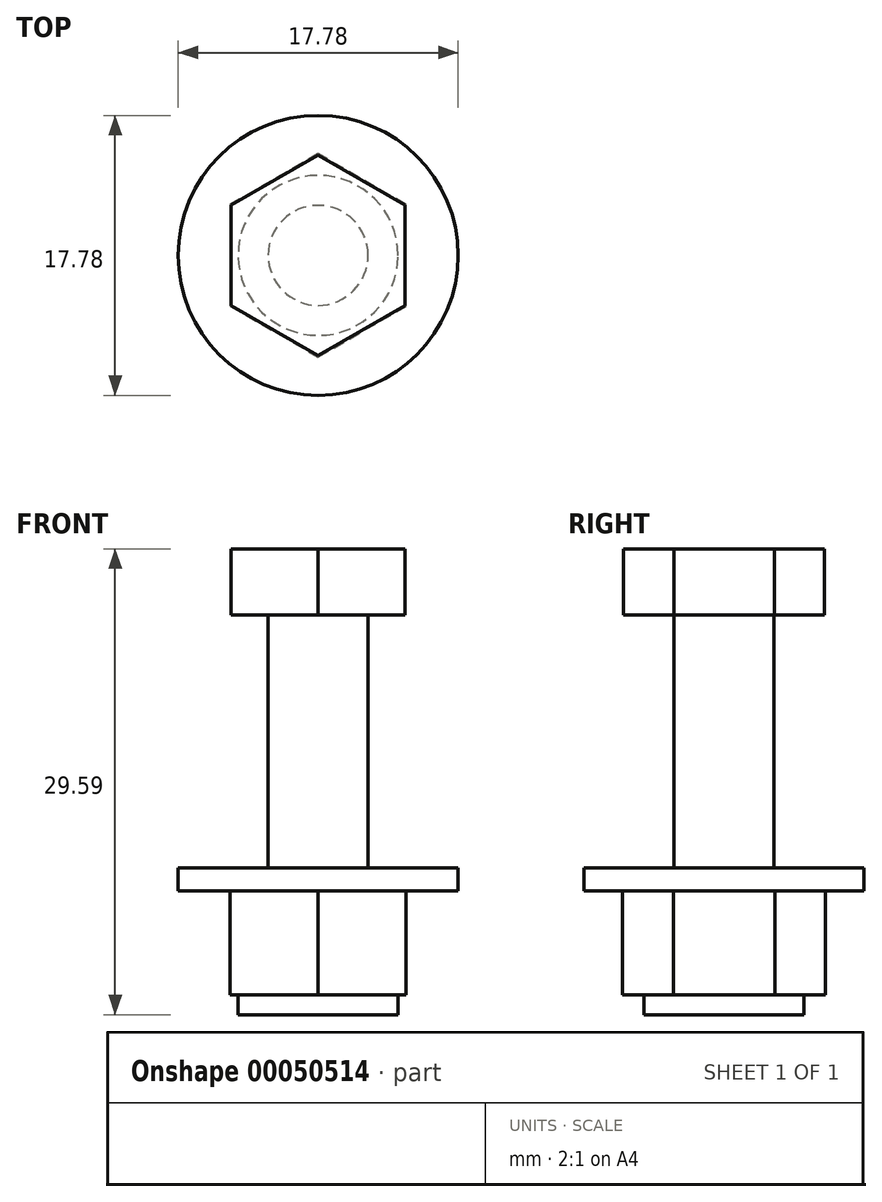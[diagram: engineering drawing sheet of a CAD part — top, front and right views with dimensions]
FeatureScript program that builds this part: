
annotation { "Feature Type Name" : "Feature", "Feature Type Description" : "" }
export const myFeature = defineFeature(function(context is Context, id is Id, definition is map)
    precondition{}
    {
        {
            var Q0;
            Q0=qCreatedBy(makeId("Top.planeOp"),FACE);
            var sketch = newSketch(context, id + "F0", { "sketchPlane" : qUnion([Q0])});
            skCircle(sketch, "E0", {"center": v(0, 0) * mm, "radius": 3.18 * mm});
            skSolve(sketch);
        }
        {
            var Q0;
            Q0 = qSketchRegion(id + "F0", true);
            extrude(context, id + "F1", {"entities" : qUnion([Q0]), "oppositeDirection" : true, "depth" : 25.4 * mm});
        }
        {
            var Q0;
            Q0=makeQuery(id+"F1.opExtrude","CAP_FACE",FACE,{"disambiguationData":[OSD([sQuery(id+"F0.wireOp",EDGE,"E0")])],"isStart":true});
            var sketch = newSketch(context, id + "F2", { "sketchPlane" : qUnion([Q0])});
            skCircle(sketch, "E1.cCircle", {"center": v(0, 0) * mm, "radius": 5.52 * mm, "construction": true});
            skLineSegment(sketch, "E1.0", {"start": v(0, 6.38) * mm, "end": v(5.52, 3.19) * mm});
            skLineSegment(sketch, "E1.1", {"start": v(5.52, 3.19) * mm, "end": v(5.52, -3.19) * mm});
            skLineSegment(sketch, "E1.2", {"start": v(5.52, -3.19) * mm, "end": v(0, -6.38) * mm});
            skLineSegment(sketch, "E1.3", {"start": v(0, -6.38) * mm, "end": v(-5.52, -3.19) * mm});
            skLineSegment(sketch, "E1.4", {"start": v(-5.52, -3.19) * mm, "end": v(-5.52, 3.19) * mm});
            skLineSegment(sketch, "E1.5", {"start": v(-5.52, 3.19) * mm, "end": v(0, 6.38) * mm});
            skPoint(sketch, "E1.0.midPoint", {"position": v(2.76, 4.78) * mm});
            skSolve(sketch);
        }
        {
            var Q0;
            Q0 = qSketchRegion(id + "F2", true);
            extrude(context, id + "F3", {"entities" : qUnion([Q0]), "operationType" : NewBodyOperationType.ADD, "depth" : 4.2 * mm});
        }
        {
            var Q0;
            Q0=makeQuery(id+"F1.opExtrude","CAP_FACE",FACE,{"disambiguationData":[OSD([sQuery(id+"F0.wireOp",EDGE,"E0")])],"isStart":false});
            var sketch = newSketch(context, id + "F4", { "sketchPlane" : qUnion([Q0])});
            skCircle(sketch, "E2.cCircle", {"center": v(0, 0) * mm, "radius": 5.59 * mm, "construction": true});
            skLineSegment(sketch, "E2.0", {"start": v(0, 6.45) * mm, "end": v(5.59, 3.23) * mm});
            skLineSegment(sketch, "E2.1", {"start": v(5.59, 3.23) * mm, "end": v(5.59, -3.23) * mm});
            skLineSegment(sketch, "E2.2", {"start": v(5.59, -3.23) * mm, "end": v(0, -6.45) * mm});
            skLineSegment(sketch, "E2.3", {"start": v(0, -6.45) * mm, "end": v(-5.59, -3.23) * mm});
            skLineSegment(sketch, "E2.4", {"start": v(-5.59, -3.23) * mm, "end": v(-5.59, 3.23) * mm});
            skLineSegment(sketch, "E2.5", {"start": v(-5.59, 3.23) * mm, "end": v(0, 6.45) * mm});
            skPoint(sketch, "E2.0.midPoint", {"position": v(2.8, 4.84) * mm});
            skSolve(sketch);
        }
        {
            var Q0;
            Q0 = qSketchRegion(id + "F4", true);
            extrude(context, id + "F5", {"entities" : qUnion([Q0]), "operationType" : NewBodyOperationType.ADD, "oppositeDirection" : true, "depth" : 7.87 * mm});
        }
        {
            var Q0;
            Q0=makeQuery(id+"F5.opExtrude","CAP_FACE",FACE,{"disambiguationData":[OSD([sQuery(id+"F4.wireOp",EDGE,"E2.0"),sQuery(id+"F4.wireOp",EDGE,"E2.1"),sQuery(id+"F4.wireOp",EDGE,"E2.2"),sQuery(id+"F4.wireOp",EDGE,"E2.3"),sQuery(id+"F4.wireOp",EDGE,"E2.4"),sQuery(id+"F4.wireOp",EDGE,"E2.5")])],"isStart":false});
            var sketch = newSketch(context, id + "F6", { "sketchPlane" : qUnion([Q0])});
            skCircle(sketch, "E3", {"center": v(0, 0) * mm, "radius": 8.9 * mm});
            skSolve(sketch);
        }
        {
            var Q0;
            Q0 = qSketchRegion(id + "F6", true);
            extrude(context, id + "F7", {"entities" : qUnion([Q0]), "operationType" : NewBodyOperationType.ADD, "depth" : 1.45 * mm});
        }
        {
            var Q0;
            Q0=makeQuery(id+"F5.boolean.opBoolean","MERGE",FACE,{"derivedFrom":[makeQuery(id+"F1.opExtrude","CAP_FACE",FACE,{"disambiguationData":[OSD([sQuery(id+"F0.wireOp",EDGE,"E0")])],"isStart":false}),makeQuery(id+"F5.opExtrude","CAP_FACE",FACE,{"disambiguationData":[OSD([sQuery(id+"F4.wireOp",EDGE,"E2.0"),sQuery(id+"F4.wireOp",EDGE,"E2.1"),sQuery(id+"F4.wireOp",EDGE,"E2.2"),sQuery(id+"F4.wireOp",EDGE,"E2.3"),sQuery(id+"F4.wireOp",EDGE,"E2.4"),sQuery(id+"F4.wireOp",EDGE,"E2.5")])],"isStart":true})]});
            var sketch = newSketch(context, id + "F8", { "sketchPlane" : qUnion([Q0])});
            skCircle(sketch, "E4", {"center": v(0, 0) * mm, "radius": 5.08 * mm});
            skLineSegment(sketch, "E5.0.0", {"start": v(5.59, 3.23) * mm, "end": v(0, 6.45) * mm});
            skLineSegment(sketch, "E5.0.1", {"start": v(0, 6.45) * mm, "end": v(-5.59, 3.23) * mm});
            skLineSegment(sketch, "E5.0.2", {"start": v(-5.59, 3.23) * mm, "end": v(-5.59, -3.23) * mm});
            skLineSegment(sketch, "E5.0.3", {"start": v(-5.59, -3.23) * mm, "end": v(0, -6.45) * mm});
            skLineSegment(sketch, "E5.0.4", {"start": v(0, -6.45) * mm, "end": v(5.59, -3.23) * mm});
            skLineSegment(sketch, "E5.0.5", {"start": v(5.59, -3.23) * mm, "end": v(5.59, 3.23) * mm});
            skSolve(sketch);
        }
        {
            var Q0;
            Q0 = qSketchRegion(id + "F8", true);
            extrude(context, id + "F9", {"entities" : qUnion([Q0]), "operationType" : NewBodyOperationType.REMOVE, "oppositeDirection" : true, "depth" : 1.27 * mm});
        }
    });
